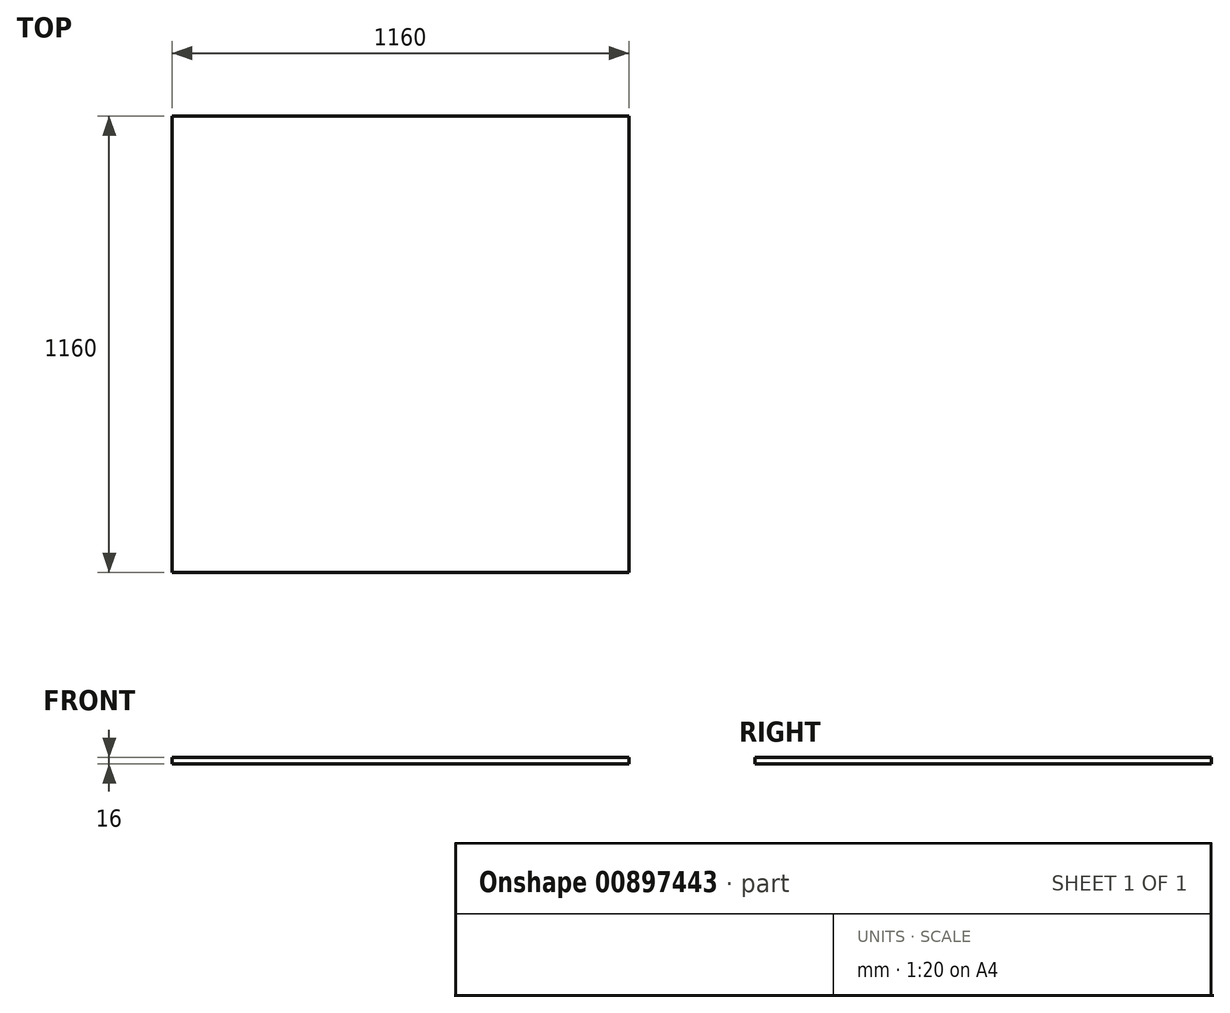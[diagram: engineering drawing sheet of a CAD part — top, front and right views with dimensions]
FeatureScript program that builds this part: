
annotation { "Feature Type Name" : "Feature", "Feature Type Description" : "" }
export const myFeature = defineFeature(function(context is Context, id is Id, definition is map)
    precondition{}
    {
        {
            var Q0;
            Q0=qCreatedBy(makeId("Top.planeOp"),FACE);
            var sketch = newSketch(context, id + "F0", { "sketchPlane" : qUnion([Q0])});
            skLineSegment(sketch, "E0.bottom", {"start": v(580, -580) * mm, "end": v(-580, -580) * mm});
            skLineSegment(sketch, "E0.top", {"start": v(580, 580) * mm, "end": v(-580, 580) * mm});
            skLineSegment(sketch, "E0.left", {"start": v(580, -580) * mm, "end": v(580, 580) * mm});
            skLineSegment(sketch, "E0.right", {"start": v(-580, -580) * mm, "end": v(-580, 580) * mm});
            skPoint(sketch, "E0.middle", {"position": v(0, 0) * mm});
            skSolve(sketch);
        }
        {
            var Q0;
            Q0=makeQuery(id+"F0.imprint","IMPRINT",FACE,{"disambiguationData":[TD([[makeQuery(id+"F0.imprint","IMPRINT",EDGE,{"derivedFrom":sQuery(id+"F0.wireOp",EDGE,"E0.bottom")}),-1.0]])]});
            extrude(context, id + "F1", {"entities" : qUnion([Q0]), "depth" : 16 * mm, "offsetDistance" : 25 * mm});
        }
    });
